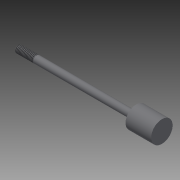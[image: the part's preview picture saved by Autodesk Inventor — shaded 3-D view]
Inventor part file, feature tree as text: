
AUTODESK INVENTOR PART (.ipt)
format: ipt  version: 2014 (Build 180170000, 170)  size: 125,440 bytes
history: native  units: in
note: dims shown in document units (in); Inventor stores cm internally (conversion verified against a paired STEP export)
features: other x49, revolve x3, sketch x3, thread x1
ambient origin geometry x8: Origin, YZ Plane, XZ Plane, XY Plane, X Axis, Y Axis, Z Axis, Center Point
bodies: Solid1 (feature_tree)
feature tree (56):
  revolve  "Revolution1"  [1 undecoded]
  thread  "Thread1"  [1 undecoded]
  revolve  "Revolution2"  [1 undecoded]
  revolve  "Revolution3"  [1 undecoded]
  other  "h1_XY"
  other  "h1_YZ"
  other  "h1_ZX"
  other  "h1_X"
  other  "h1_Y"
  other  "h1_Z"
  other  "h1_Center"
  other  "h2_XY"
  other  "h2_YZ"
  other  "h2_ZX"
  other  "h2_X"
  other  "h2_Y"
  other  "h2_Z"
  other  "h2_Center"
  other  "k1_XY"
  other  "k1_YZ"
  other  "k1_ZX"
  other  "k1_X"
  other  "k1_Y"
  other  "k1_Z"
  other  "k1_Center"
  other  "k2_XY"
  other  "k2_YZ"
  other  "k2_ZX"
  other  "k2_X"
  other  "k2_Y"
  other  "k2_Z"
  other  "k2_Center"
  other  "start_XY"
  other  "start_YZ"
  other  "start_ZX"
  other  "start_X"
  other  "start_Y"
  other  "start_Z"
  other  "start_Center"
  other  "to_prc_XY"
  other  "to_prc_YZ"
  other  "to_prc_ZX"
  other  "to_prc_X"
  other  "to_prc_Y"
  other  "to_prc_Z"
  other  "to_prc_Center"
  other  "to_rod_guide_XY"
  other  "to_rod_guide_YZ"
  other  "to_rod_guide_ZX"
  other  "to_rod_guide_X"
  other  "to_rod_guide_Y"
  other  "to_rod_guide_Z"
  other  "to_rod_guide_Center"
  sketch  "Sketch_3"  dims[d0=360.0deg d1=0.49in d2=3.291in d3=360.0deg]
  sketch  "Sketch_17"
  sketch  "Sketch_12"  dims[d4=360.0deg]
note: 4 required parameter values undecoded (feature->parameter linkage not recoverable at this tier; creation-order binding heuristic only, values carry confidence <= 0.55)